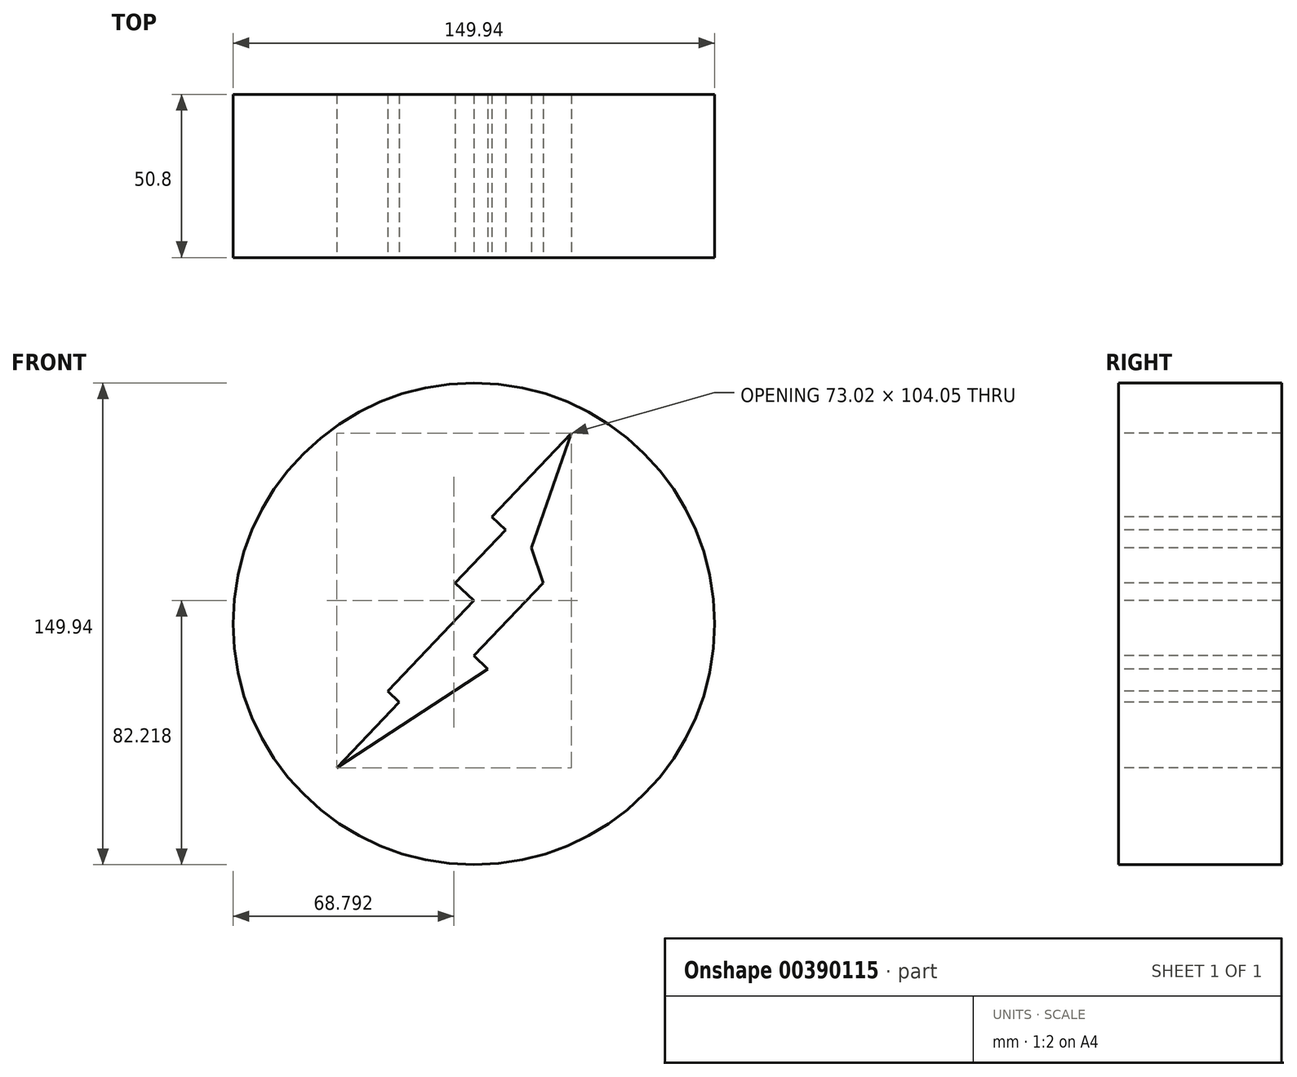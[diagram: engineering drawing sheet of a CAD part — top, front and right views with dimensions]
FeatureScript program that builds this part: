
annotation { "Feature Type Name" : "Feature", "Feature Type Description" : "" }
export const myFeature = defineFeature(function(context is Context, id is Id, definition is map)
    precondition{}
    {
        {
            var Q0;
            Q0=qCreatedBy(makeId("Front.planeOp"),FACE);
            var sketch = newSketch(context, id + "F0", { "sketchPlane" : qUnion([Q0])});
            skCircle(sketch, "E0", {"center": v(0, 0) * mm, "radius": 74.97 * mm});
            skSolve(sketch);
        }
        {
            var Q0;
            Q0 = qSketchRegion(id + "F0", true);
            extrude(context, id + "F1", {"entities" : qUnion([Q0]), "depth" : 50.8 * mm});
        }
        {
            var Q0;
            Q0=makeQuery(id+"F1.opExtrude","CAP_FACE",FACE,{"disambiguationData":[OSD([sQuery(id+"F0.wireOp",EDGE,"E0")])],"isStart":false});
            var sketch = newSketch(context, id + "F2", { "sketchPlane" : qUnion([Q0])});
            skLineSegment(sketch, "E1", {"start": v(30.33, 59.27) * mm, "end": v(5.57, 33.27) * mm});
            skLineSegment(sketch, "E2", {"start": v(5.57, 33.27) * mm, "end": v(9.88, 29.17) * mm});
            skLineSegment(sketch, "E3", {"start": v(9.88, 29.17) * mm, "end": v(-5.8, 12.7) * mm});
            skLineSegment(sketch, "E4", {"start": v(-5.8, 12.7) * mm, "end": v(0, 7.19) * mm});
            skLineSegment(sketch, "E5", {"start": v(0, 7.19) * mm, "end": v(-26.8, -20.96) * mm});
            skLineSegment(sketch, "E6", {"start": v(-26.8, -20.96) * mm, "end": v(-23.24, -24.36) * mm});
            skLineSegment(sketch, "E7", {"start": v(-23.24, -24.36) * mm, "end": v(-42.69, -44.78) * mm});
            skLineSegment(sketch, "E8", {"start": v(-42.69, -44.78) * mm, "end": v(4.33, -14.08) * mm});
            skLineSegment(sketch, "E9", {"start": v(4.33, -14.08) * mm, "end": v(0, -9.96) * mm});
            skLineSegment(sketch, "E10", {"start": v(0, -9.96) * mm, "end": v(21.58, 12.7) * mm});
            skLineSegment(sketch, "E11", {"start": v(21.58, 12.7) * mm, "end": v(17.95, 23.68) * mm});
            skLineSegment(sketch, "E12", {"start": v(17.95, 23.68) * mm, "end": v(30.33, 59.27) * mm});
            skSolve(sketch);
        }
        {
            var Q0;
            Q0=makeQuery(id+"F2.imprint","IMPRINT",FACE,{"disambiguationData":[TD([[makeQuery(id+"F2.imprint","IMPRINT",EDGE,{"derivedFrom":sQuery(id+"F2.wireOp",EDGE,"E1")}),1.0]])]});
            extrude(context, id + "F3", {"entities" : qUnion([Q0]), "operationType" : NewBodyOperationType.REMOVE, "oppositeDirection" : true, "depth" : 76.2 * mm});
        }
    });
